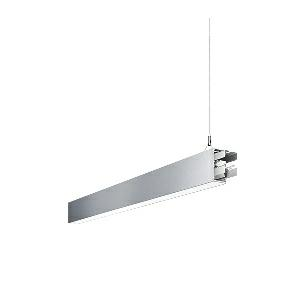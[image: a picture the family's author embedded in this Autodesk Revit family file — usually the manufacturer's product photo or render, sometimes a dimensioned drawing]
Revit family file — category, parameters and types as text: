
# Revit family: idoo_line_-_ilp_2000_830_d_mid_00805718_fc94
name_source: partatom
category: Lighting Fixtures
units: mm (PartAtom-declared; Revit-internal decimal feet)

## family parameters
Cut with Voids When Loaded = No
Host = Face
Light Source = No
Part Type = Normal
Room Calculation Point = No
Round Connector Dimension = Use Diameter
Shared = No

## types (1)
- IDOO.line - ILP 2000/830/D MID (1 x LED, 2250 lm, 3000K)
    Apparent Load = 17 VA
    Approval mark = CE
    CIE Flux Codes = 66 91 98 40 100
    Color Rendering = 80-89
    Color Temperature = 3000K
    Control Gear = Electronic ballast
    Default Elevation = 1800 mm
    Description = ILP 2000/830/D|Suspended luminaire|light source: LED|connected load: 220-240 V, 50/60 Hz|Power consumption: approx. 17 W|standby: approx. 0,20|luminous flux: 2250 lm|luminous efficacy: 132 lm/W|light distribution: Direct/indirect|direct ratio: approx. 40 %|colour temperature: Warm white, ca. 3000 K|color rendering index (CRI): >= 80|chromaticity tolerance:  3 SDCM|System of protection: IP 40|technology: Continuously dimmable|luminaire body|material: Sectional aluminium|colour: Silver|lamp cover: Acrylic (PMMA), Clear|mains lead: 1,0 m With free stranded wires|Fastening: Steel cable 0.3 - 0.7 m|glare control: Prism aperture|luminance(L65): <= 2700 cd/m|unified glare rating(4H 8H): <=  16|special features: DALI Load 1x, TouchDIM - dimming via standard switch, Through-wired, up to 18 m on one mains connection, Flicker-free, Suitable as emergency lighting, Mechanical and electrical connection of the individual modules without tools|
    Frequency = 50 Hz
    Height = 110 mm
    Lamp = 1 x LED
    Lamp Light Flux = 2250 lm
    Lamp count = 1
    Length = 842 mm
    Luminous efficacy = 132 lm/W
    Manufacturer = Waldmann
    ModVariant = No
    Model = 00805718
    Mounting Place = Ceiling
    Mounting Type = Pendant
    Number of Poles = 1
    OnlyDefault = Yes
    Power Factor = 1
    Product Name = IDOO.line - ILP 2000/830/D MID
    Product group = Suspended luminaire
    ProductGroupID = 9
    Protection Class = Protection class I
    Protection Degree = IP 40
    RLX_Detail_Level = 1
    RLX_Emergency_Light_Flux = 0 lm
    RLX_Emergency_Type = 0
    RLX_Emergency_Type_DB = No
    RlxData = <blob elided: 19417 chars, md5=532f730b>
    Socket = socket
    Standby Power = 0 W
    System Light Flux = 2250 lm
    System Power = 17 W
    Type Comments = Product without accessories
    Type Image = 113299000-00692561.jpg
    URL = http://relux.com
    VarID = ---
    Voltage = 230 V
    Voltage Range = 220-240 V
    Weight = 0.00 kg
    Width = 60 mm  [stored 0.19685 ft]

note: [stored X ft] marks values corroborated as IEEE doubles in the binary element streams (Revit-internal decimal feet)

## geometry (parser evidence)
native form markers: Blend x4, Sweep x14
no freeform markers — native parametric forms only
